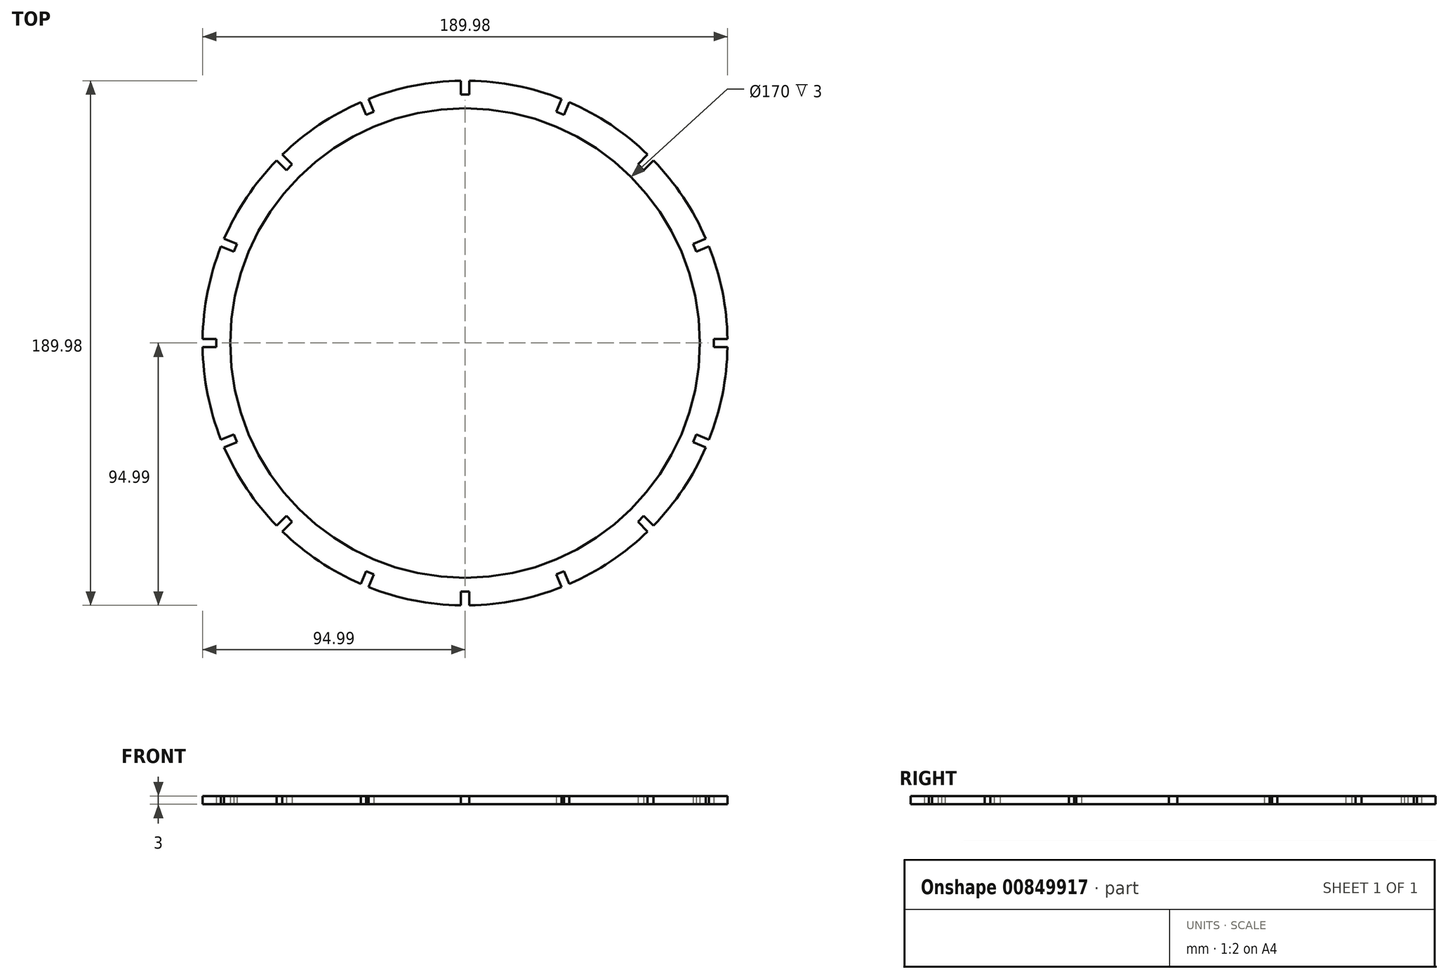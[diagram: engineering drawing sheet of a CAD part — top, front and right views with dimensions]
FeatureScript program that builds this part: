
annotation { "Feature Type Name" : "Feature", "Feature Type Description" : "" }
export const myFeature = defineFeature(function(context is Context, id is Id, definition is map)
    precondition{}
    {
        {
            var Q0;
            Q0=qCreatedBy(makeId("Top.planeOp"),FACE);
            var sketch = newSketch(context, id + "F0", { "sketchPlane" : qUnion([Q0])});
            skCircle(sketch, "E0", {"center": v(0, 0) * mm, "radius": 85 * mm});
            skCircle(sketch, "E1", {"center": v(0, 0) * mm, "radius": 95 * mm});
            skLineSegment(sketch, "E2", {"start": v(-1.5, -90) * mm, "end": v(1.5, -90) * mm});
            skLineSegment(sketch, "E3", {"start": v(-1.5, -90) * mm, "end": v(-1.5, -94.99) * mm});
            skLineSegment(sketch, "E4", {"start": v(1.5, -90) * mm, "end": v(1.5, -94.99) * mm});
            skLineSegment(sketch, "E5.1.0", {"start": v(33.06, -83.72) * mm, "end": v(35.83, -82.58) * mm});
            skLineSegment(sketch, "E5.1.1", {"start": v(33.06, -83.72) * mm, "end": v(34.96, -88.33) * mm});
            skLineSegment(sketch, "E5.1.2", {"start": v(35.83, -82.58) * mm, "end": v(37.74, -87.18) * mm});
            skLineSegment(sketch, "E5.2.0", {"start": v(62.58, -64.7) * mm, "end": v(64.7, -62.58) * mm});
            skLineSegment(sketch, "E5.2.1", {"start": v(62.58, -64.7) * mm, "end": v(66.1, -68.23) * mm});
            skLineSegment(sketch, "E5.2.2", {"start": v(64.7, -62.58) * mm, "end": v(68.23, -66.1) * mm});
            skLineSegment(sketch, "E5.3.0", {"start": v(82.58, -35.83) * mm, "end": v(83.72, -33.06) * mm});
            skLineSegment(sketch, "E5.3.1", {"start": v(82.58, -35.83) * mm, "end": v(87.18, -37.74) * mm});
            skLineSegment(sketch, "E5.3.2", {"start": v(83.72, -33.06) * mm, "end": v(88.33, -34.96) * mm});
            skLineSegment(sketch, "E5.4.0", {"start": v(90, -1.5) * mm, "end": v(90, 1.5) * mm});
            skLineSegment(sketch, "E5.4.1", {"start": v(90, -1.5) * mm, "end": v(94.99, -1.5) * mm});
            skLineSegment(sketch, "E5.4.2", {"start": v(90, 1.5) * mm, "end": v(94.99, 1.5) * mm});
            skLineSegment(sketch, "E5.5.0", {"start": v(83.72, 33.06) * mm, "end": v(82.58, 35.83) * mm});
            skLineSegment(sketch, "E5.5.1", {"start": v(83.72, 33.06) * mm, "end": v(88.33, 34.96) * mm});
            skLineSegment(sketch, "E5.5.2", {"start": v(82.58, 35.83) * mm, "end": v(87.18, 37.74) * mm});
            skLineSegment(sketch, "E5.6.0", {"start": v(64.7, 62.58) * mm, "end": v(62.58, 64.7) * mm});
            skLineSegment(sketch, "E5.6.1", {"start": v(64.7, 62.58) * mm, "end": v(68.23, 66.1) * mm});
            skLineSegment(sketch, "E5.6.2", {"start": v(62.58, 64.7) * mm, "end": v(66.1, 68.23) * mm});
            skLineSegment(sketch, "E5.7.0", {"start": v(35.83, 82.58) * mm, "end": v(33.06, 83.72) * mm});
            skLineSegment(sketch, "E5.7.1", {"start": v(35.83, 82.58) * mm, "end": v(37.74, 87.18) * mm});
            skLineSegment(sketch, "E5.7.2", {"start": v(33.06, 83.72) * mm, "end": v(34.96, 88.33) * mm});
            skLineSegment(sketch, "E5.8.0", {"start": v(1.5, 90) * mm, "end": v(-1.5, 90) * mm});
            skLineSegment(sketch, "E5.8.1", {"start": v(1.5, 90) * mm, "end": v(1.5, 94.99) * mm});
            skLineSegment(sketch, "E5.8.2", {"start": v(-1.5, 90) * mm, "end": v(-1.5, 94.99) * mm});
            skLineSegment(sketch, "E5.9.0", {"start": v(-33.06, 83.72) * mm, "end": v(-35.83, 82.58) * mm});
            skLineSegment(sketch, "E5.9.1", {"start": v(-33.06, 83.72) * mm, "end": v(-34.96, 88.33) * mm});
            skLineSegment(sketch, "E5.9.2", {"start": v(-35.83, 82.58) * mm, "end": v(-37.74, 87.18) * mm});
            skLineSegment(sketch, "E5.10.0", {"start": v(-62.58, 64.7) * mm, "end": v(-64.7, 62.58) * mm});
            skLineSegment(sketch, "E5.10.1", {"start": v(-62.58, 64.7) * mm, "end": v(-66.1, 68.23) * mm});
            skLineSegment(sketch, "E5.10.2", {"start": v(-64.7, 62.58) * mm, "end": v(-68.23, 66.1) * mm});
            skLineSegment(sketch, "E5.11.0", {"start": v(-82.58, 35.83) * mm, "end": v(-83.72, 33.06) * mm});
            skLineSegment(sketch, "E5.11.1", {"start": v(-82.58, 35.83) * mm, "end": v(-87.18, 37.74) * mm});
            skLineSegment(sketch, "E5.11.2", {"start": v(-83.72, 33.06) * mm, "end": v(-88.33, 34.96) * mm});
            skLineSegment(sketch, "E5.12.0", {"start": v(-90, 1.5) * mm, "end": v(-90, -1.5) * mm});
            skLineSegment(sketch, "E5.12.1", {"start": v(-90, 1.5) * mm, "end": v(-94.99, 1.5) * mm});
            skLineSegment(sketch, "E5.12.2", {"start": v(-90, -1.5) * mm, "end": v(-94.99, -1.5) * mm});
            skLineSegment(sketch, "E5.13.0", {"start": v(-83.72, -33.06) * mm, "end": v(-82.58, -35.83) * mm});
            skLineSegment(sketch, "E5.13.1", {"start": v(-83.72, -33.06) * mm, "end": v(-88.33, -34.96) * mm});
            skLineSegment(sketch, "E5.13.2", {"start": v(-82.58, -35.83) * mm, "end": v(-87.18, -37.74) * mm});
            skLineSegment(sketch, "E5.14.0", {"start": v(-64.7, -62.58) * mm, "end": v(-62.58, -64.7) * mm});
            skLineSegment(sketch, "E5.14.1", {"start": v(-64.7, -62.58) * mm, "end": v(-68.23, -66.1) * mm});
            skLineSegment(sketch, "E5.14.2", {"start": v(-62.58, -64.7) * mm, "end": v(-66.1, -68.23) * mm});
            skLineSegment(sketch, "E5.15.0", {"start": v(-35.83, -82.58) * mm, "end": v(-33.06, -83.72) * mm});
            skLineSegment(sketch, "E5.15.1", {"start": v(-35.83, -82.58) * mm, "end": v(-37.74, -87.18) * mm});
            skLineSegment(sketch, "E5.15.2", {"start": v(-33.06, -83.72) * mm, "end": v(-34.96, -88.33) * mm});
            skSolve(sketch);
        }
        {
            var Q0;
            Q0=makeQuery(id+"F0.imprint","IMPRINT",FACE,{"disambiguationData":[TD([[makeQuery(id+"F0.imprint","IMPRINT",EDGE,{"derivedFrom":sQuery(id+"F0.wireOp",EDGE,"E0")}),-1.0]])]});
            extrude(context, id + "F1", {"entities" : qUnion([Q0]), "depth" : 3 * mm, "offsetDistance" : 25 * mm});
        }
    });
